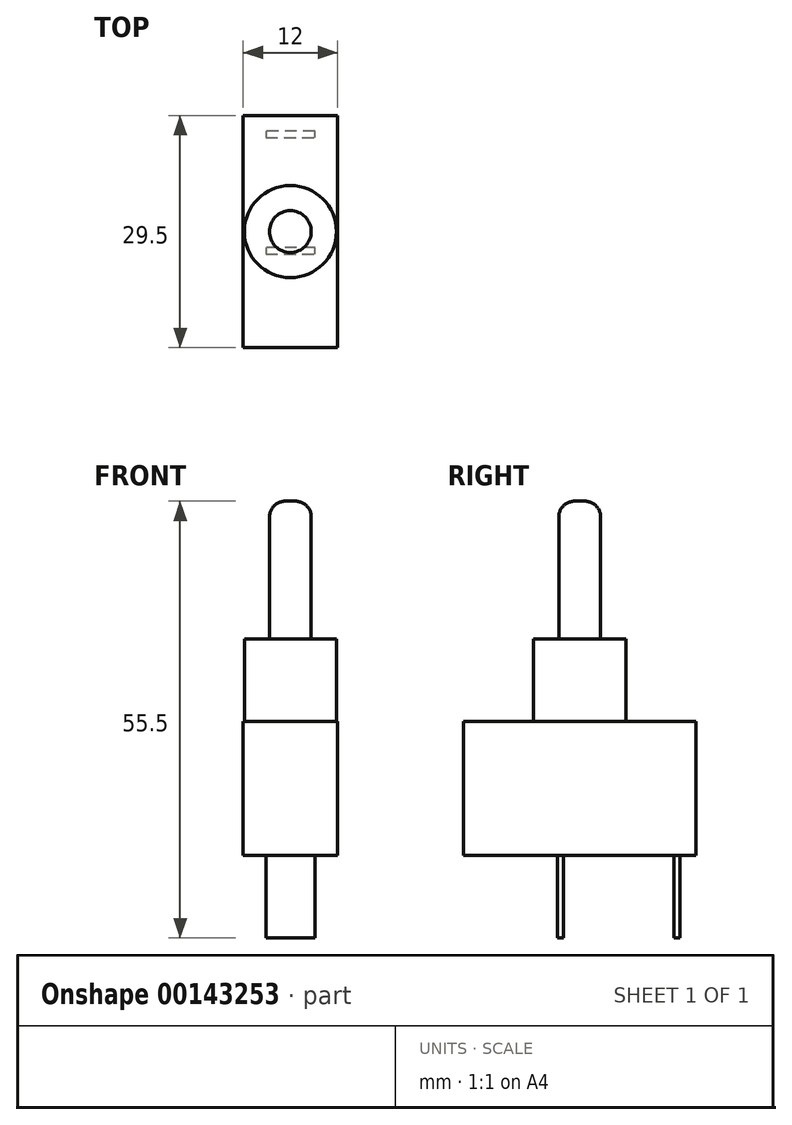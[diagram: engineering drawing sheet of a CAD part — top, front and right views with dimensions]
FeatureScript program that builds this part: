
annotation { "Feature Type Name" : "Feature", "Feature Type Description" : "" }
export const myFeature = defineFeature(function(context is Context, id is Id, definition is map)
    precondition{}
    {
        {
            var Q0;
            Q0=qCreatedBy(makeId("Top.planeOp"),FACE);
            var sketch = newSketch(context, id + "F0", { "sketchPlane" : qUnion([Q0])});
            skLineSegment(sketch, "E0.bottom", {"start": v(-3.85, 9.69) * mm, "end": v(8.15, 9.69) * mm});
            skLineSegment(sketch, "E0.top", {"start": v(-3.85, -19.81) * mm, "end": v(8.15, -19.81) * mm});
            skLineSegment(sketch, "E0.left", {"start": v(-3.85, 9.69) * mm, "end": v(-3.85, -19.81) * mm});
            skLineSegment(sketch, "E0.right", {"start": v(8.15, 9.69) * mm, "end": v(8.15, -19.81) * mm});
            skCircle(sketch, "E1", {"center": v(2.15, -5.06) * mm, "radius": 5.85 * mm});
            skPoint(sketch, "E1.centerSnap0", {"position": v(2.15, -19.81) * mm});
            skPoint(sketch, "E1.centerSnap1", {"position": v(-3.85, -5.06) * mm});
            skSolve(sketch);
        }
        {
            var Q0;
            Q0=makeQuery(id+"F0.imprint","IMPRINT",FACE,{"disambiguationData":[TD([[makeQuery(id+"F0.imprint","IMPRINT",EDGE,{"derivedFrom":sQuery(id+"F0.wireOp",EDGE,"E0.bottom")}),-1.0]])]});
            var Q1;
            Q1=makeQuery(id+"F0.imprint","IMPRINT",FACE,{"disambiguationData":[TD([[makeQuery(id+"F0.imprint","IMPRINT",EDGE,{"derivedFrom":sQuery(id+"F0.wireOp",EDGE,"E1")}),1.0]])]});
            extrude(context, id + "F1", {"entities" : qUnion([Q0, Q1]), "oppositeDirection" : true, "depth" : 17 * mm});
        }
        {
            var Q0;
            Q0=makeQuery(id+"F0.imprint","IMPRINT",FACE,{"disambiguationData":[TD([[makeQuery(id+"F0.imprint","IMPRINT",EDGE,{"derivedFrom":sQuery(id+"F0.wireOp",EDGE,"E1")}),1.0]])]});
            extrude(context, id + "F2", {"entities" : qUnion([Q0]), "operationType" : NewBodyOperationType.ADD, "depth" : 10.5 * mm});
        }
        {
            var Q0;
            Q0=makeQuery(id+"F2.opExtrude","CAP_FACE",FACE,{"disambiguationData":[OSD([sQuery(id+"F0.wireOp",EDGE,"E1")])],"isStart":false});
            var sketch = newSketch(context, id + "F3", { "sketchPlane" : qUnion([Q0])});
            skCircle(sketch, "E2.0", {"center": v(2.15, -5.06) * mm, "radius": 5.85 * mm});
            skCircle(sketch, "E3", {"center": v(2.15, -5.06) * mm, "radius": 2.65 * mm});
            skSolve(sketch);
        }
        {
            var Q0;
            Q0=makeQuery(id+"F3.imprint","IMPRINT",FACE,{"disambiguationData":[TD([[makeQuery(id+"F3.imprint","IMPRINT",EDGE,{"derivedFrom":sQuery(id+"F3.wireOp",EDGE,"E3")}),1.0]])]});
            extrude(context, id + "F4", {"entities" : qUnion([Q0]), "operationType" : NewBodyOperationType.ADD, "depth" : 17.5 * mm});
        }
        {
            var Q0;
            Q0=makeQuery(id+"F4.opExtrude","CAP_EDGE",EDGE,{"disambiguationData":[OSD([sQuery(id+"F3.wireOp",EDGE,"E3")])],"isStart":false});
            fillet(context, id + "F5", {"entities" : qUnion([Q0]), "radius" : 2 * mm, "tangentPropagation" : true, "allowEdgeOverflow" : false});
        }
        {
            var Q0;
            Q0=makeQuery(id+"F1.opExtrude","CAP_FACE",FACE,{"disambiguationData":[OSD([sQuery(id+"F0.wireOp",EDGE,"E0.bottom"),sQuery(id+"F0.wireOp",EDGE,"E0.top"),sQuery(id+"F0.wireOp",EDGE,"E0.left"),sQuery(id+"F0.wireOp",EDGE,"E0.right")])],"isStart":false});
            var sketch = newSketch(context, id + "F6", { "sketchPlane" : qUnion([Q0])});
            skLineSegment(sketch, "E4", {"start": v(2.15, -9.69) * mm, "end": v(2.15, -7.69) * mm, "construction": true});
            skLineSegment(sketch, "E5", {"start": v(2.15, -7.69) * mm, "end": v(-0.95, -7.69) * mm});
            skLineSegment(sketch, "E6", {"start": v(2.15, -7.69) * mm, "end": v(5.25, -7.69) * mm});
            skLineSegment(sketch, "E7", {"start": v(-0.95, -7.69) * mm, "end": v(-0.95, -6.89) * mm});
            skLineSegment(sketch, "E8", {"start": v(-0.95, -6.89) * mm, "end": v(5.25, -6.89) * mm});
            skLineSegment(sketch, "E9", {"start": v(5.25, -6.89) * mm, "end": v(5.25, -7.69) * mm});
            skLineSegment(sketch, "E10", {"start": v(2.15, -6.89) * mm, "end": v(2.15, 7.11) * mm, "construction": true});
            skLineSegment(sketch, "E11", {"start": v(2.15, 7.11) * mm, "end": v(-0.95, 7.11) * mm});
            skLineSegment(sketch, "E12", {"start": v(2.15, 7.11) * mm, "end": v(5.25, 7.11) * mm});
            skLineSegment(sketch, "E13", {"start": v(-0.95, 7.11) * mm, "end": v(-0.95, 7.91) * mm});
            skLineSegment(sketch, "E14", {"start": v(-0.95, 7.91) * mm, "end": v(5.25, 7.91) * mm});
            skLineSegment(sketch, "E15", {"start": v(5.25, 7.91) * mm, "end": v(5.25, 7.11) * mm});
            skSolve(sketch);
        }
        {
            var Q0;
            Q0=makeQuery(id+"F6.imprint","IMPRINT",FACE,{"disambiguationData":[TD([[makeQuery(id+"F6.imprint","IMPRINT",EDGE,{"derivedFrom":sQuery(id+"F6.wireOp",EDGE,"E11")}),-1.0]])]});
            var Q1;
            Q1=makeQuery(id+"F6.imprint","IMPRINT",FACE,{"disambiguationData":[TD([[makeQuery(id+"F6.imprint","IMPRINT",EDGE,{"derivedFrom":sQuery(id+"F6.wireOp",EDGE,"E5")}),-1.0]])]});
            extrude(context, id + "F7", {"entities" : qUnion([Q0, Q1]), "operationType" : NewBodyOperationType.ADD, "depth" : 10.5 * mm});
        }
    });
